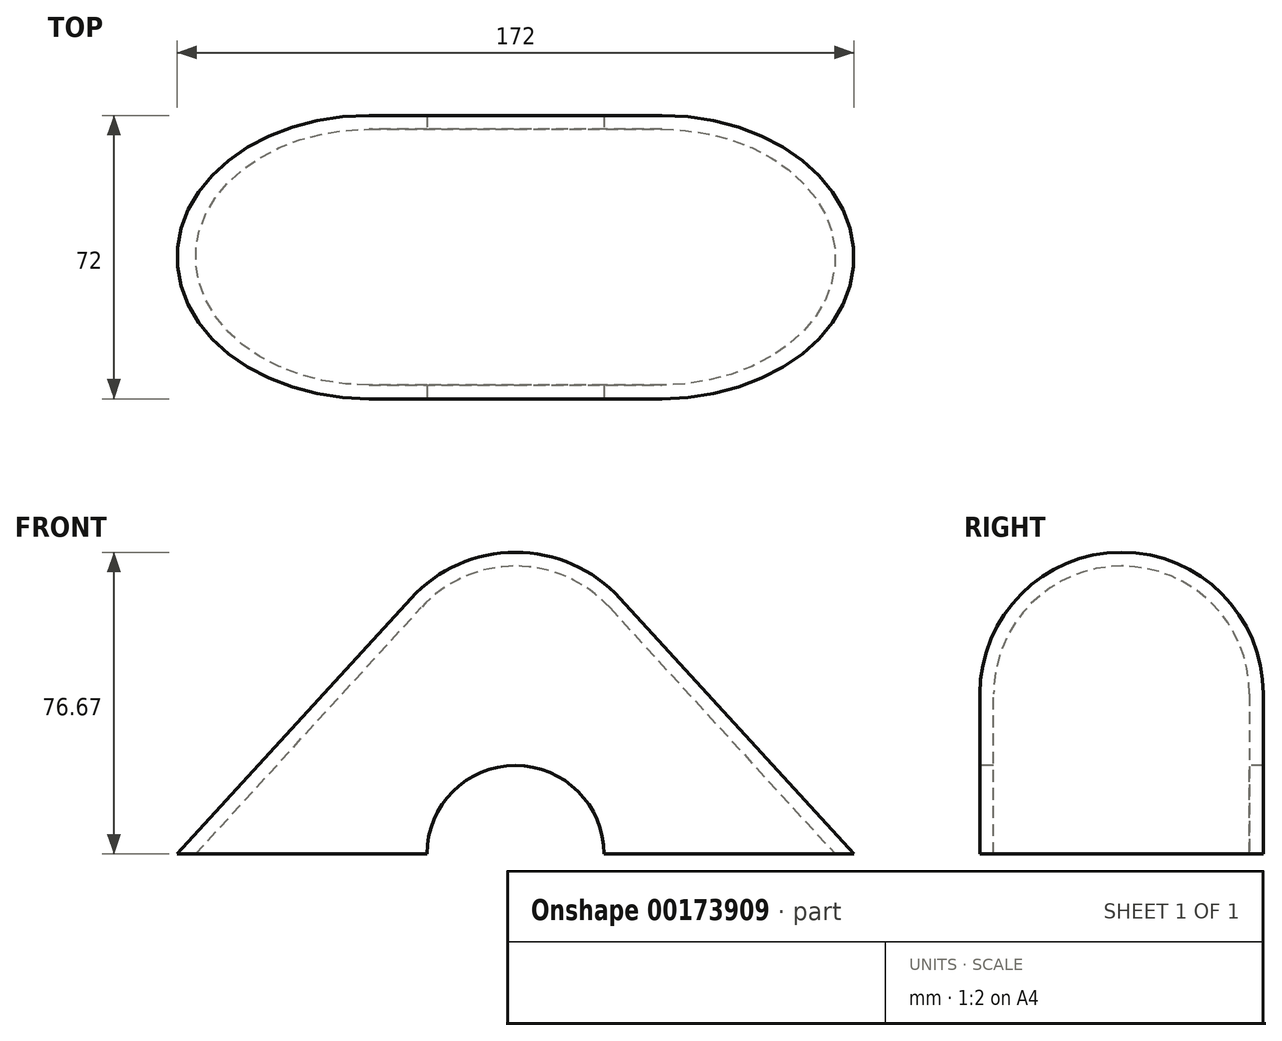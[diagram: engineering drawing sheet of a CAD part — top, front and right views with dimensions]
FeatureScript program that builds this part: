
annotation { "Feature Type Name" : "Feature", "Feature Type Description" : "" }
export const myFeature = defineFeature(function(context is Context, id is Id, definition is map)
    precondition{}
    {
        {
            var Q0;
            Q0=qCreatedBy(makeId("Front.planeOp"),FACE);
            var sketch = newSketch(context, id + "F0", { "sketchPlane" : qUnion([Q0])});
            skLineSegment(sketch, "E0", {"start": v(-86, 0) * mm, "end": v(0, 94) * mm});
            skLineSegment(sketch, "E1", {"start": v(0, 94) * mm, "end": v(86, 0) * mm});
            skLineSegment(sketch, "E2", {"start": v(86, 0) * mm, "end": v(-86, 0) * mm});
            skSolve(sketch);
        }
        {
            assignVariable(context, id + "F1", {"name" : "width", "anyValue" : 72});
        }
        {
            var Q0;
            Q0=makeQuery(id+"F0.imprint","IMPRINT",FACE,{"disambiguationData":[TD([[makeQuery(id+"F0.imprint","IMPRINT",EDGE,{"derivedFrom":sQuery(id+"F0.wireOp",EDGE,"E0")}),-1.0]])]});
            extrude(context, id + "F2", {"entities" : qUnion([Q0]), "endBound" : BoundingType.SYMMETRIC, "depth" : (getVariable(context, 'width')) * mm});
        }
        {
            var Q0;
            Q0=makeQuery(id+"F2.opExtrude","CAP_EDGE",EDGE,{"disambiguationData":[OSD([sQuery(id+"F0.wireOp",EDGE,"E0")])],"isStart":true});
            var Q1;
            Q1=makeQuery(id+"F2.opExtrude","CAP_EDGE",EDGE,{"disambiguationData":[OSD([sQuery(id+"F0.wireOp",EDGE,"E0")])],"isStart":false});
            var Q2;
            Q2=makeQuery(id+"F2.opExtrude","CAP_EDGE",EDGE,{"disambiguationData":[OSD([sQuery(id+"F0.wireOp",EDGE,"E1")])],"isStart":false});
            var Q3;
            Q3=makeQuery(id+"F2.opExtrude","CAP_EDGE",EDGE,{"disambiguationData":[OSD([sQuery(id+"F0.wireOp",EDGE,"E1")])],"isStart":true});
            var Q4;
            Q4=makeQuery(id+"F2.opExtrude","SWEPT_EDGE",EDGE,{"disambiguationData":[OSD([sQuery(id+"F0.wireOp",EDGE,"E0"),sQuery(id+"F0.wireOp",EDGE,"E1")])]});
            fillet(context, id + "F3", {"entities" : qUnion([Q0, Q1, Q2, Q3, Q4]), "radius" : (getVariable(context, 'width') / 2) * mm, "tangentPropagation" : true, "allowEdgeOverflow" : false});
        }
        {
            var Q0;
            Q0=makeQuery(id+"F2.opExtrude","CAP_FACE",FACE,{"disambiguationData":[OSD([sQuery(id+"F0.wireOp",EDGE,"E0"),sQuery(id+"F0.wireOp",EDGE,"E1"),sQuery(id+"F0.wireOp",EDGE,"E2")])],"isStart":false});
            var sketch = newSketch(context, id + "F4", { "sketchPlane" : qUnion([Q0])});
            skArc(sketch, "E3", {"start": v(22.5, 0) * mm, "mid": v(0, 22.5) * mm, "end": v(-22.5, 0) * mm});
            skSolve(sketch);
        }
        {
            var Q0;
            {var subQ0=sQuery(id+"F4.wireOp",EDGE,"E3");Q0=makeQuery(id+"F4.imprint","IMPRINT",FACE,{"disambiguationData":[TD([[makeQuery(id+"F4.imprint","IMPRINT",EDGE,{"derivedFrom":subQ0}),1.0]])]});}
            extrude(context, id + "F5", {"entities" : qUnion([Q0]), "operationType" : NewBodyOperationType.REMOVE, "endBound" : BoundingType.THROUGH_ALL, "oppositeDirection" : true, "depth" : 25 * mm});
        }
        {
            var Q0;
            Q0=makeQuery(id+"F2.opExtrude","SWEPT_FACE",FACE,{"disambiguationData":[OSD([sQuery(id+"F0.wireOp",EDGE,"E2")])]});
            var Q1;
            Q1=makeQuery(id+"F5.boolean.opBoolean","COPY",FACE,{"derivedFrom":makeQuery(id+"F5.opExtrude","SWEPT_FACE",FACE,{"disambiguationData":[OSD([sQuery(id+"F4.wireOp",EDGE,"E3")])]})});
            shell(context, id + "F6", {"entities" : qUnion([Q0, Q1]), "thickness" : 3.5 * mm});
        }
    });
